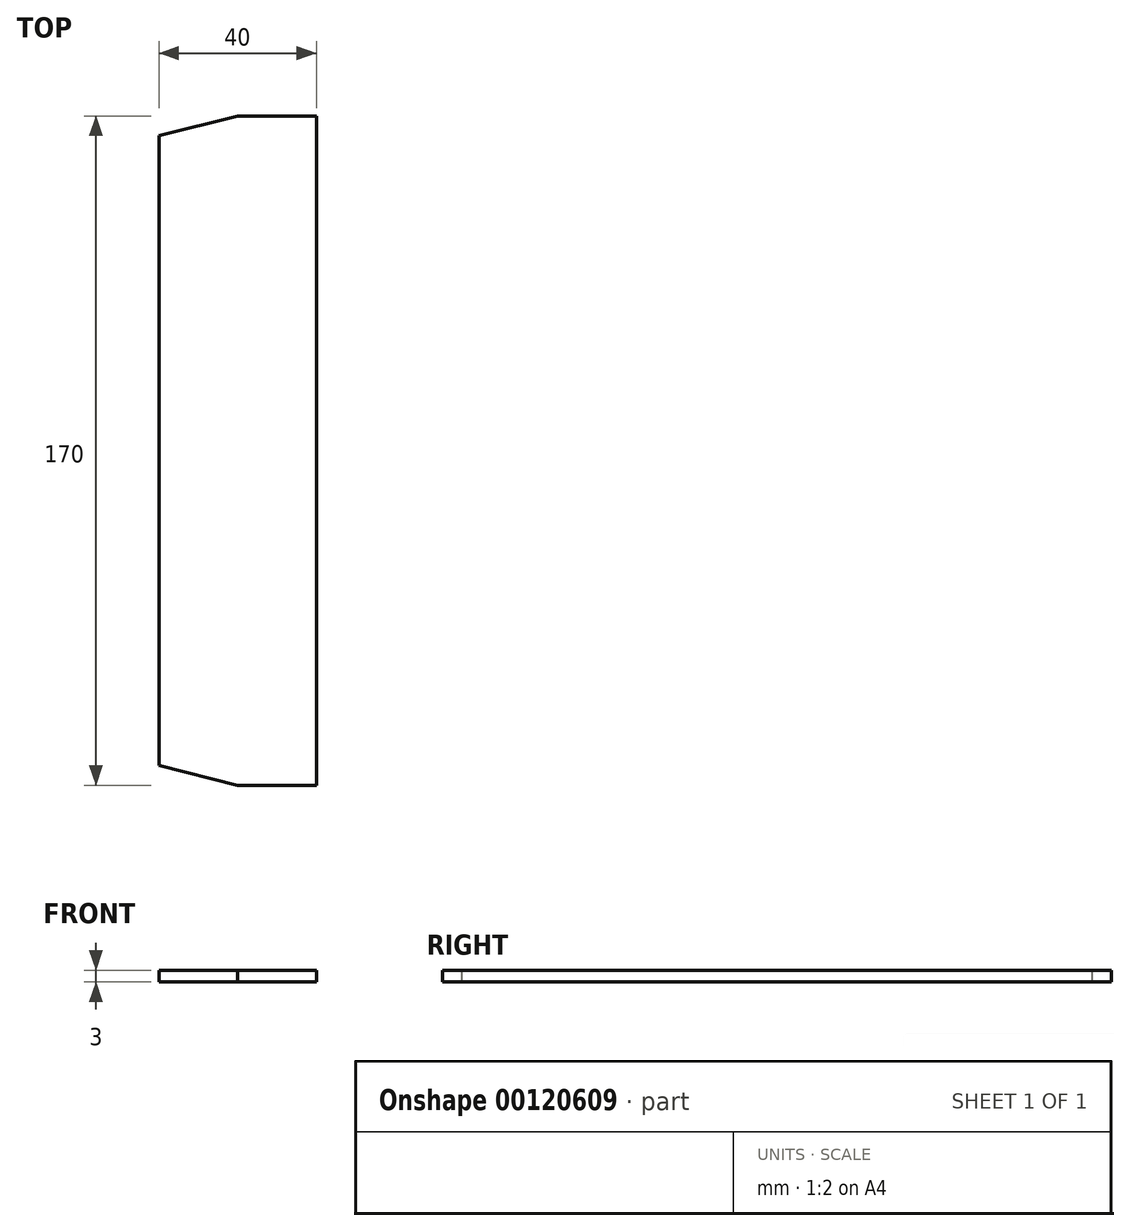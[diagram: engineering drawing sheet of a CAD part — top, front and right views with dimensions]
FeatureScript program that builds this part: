
annotation { "Feature Type Name" : "Feature", "Feature Type Description" : "" }
export const myFeature = defineFeature(function(context is Context, id is Id, definition is map)
    precondition{}
    {
        {
            var Q0;
            Q0=qCreatedBy(makeId("Top.planeOp"),FACE);
            var sketch = newSketch(context, id + "F0", { "sketchPlane" : qUnion([Q0])});
            skLineSegment(sketch, "E0.bottom", {"start": v(-59.55, 85.54) * mm, "end": v(-19.55, 85.54) * mm});
            skLineSegment(sketch, "E0.top", {"start": v(-59.55, -84.46) * mm, "end": v(-19.55, -84.46) * mm});
            skLineSegment(sketch, "E0.left", {"start": v(-59.55, 85.54) * mm, "end": v(-59.55, -84.46) * mm});
            skLineSegment(sketch, "E0.right", {"start": v(-19.55, 85.54) * mm, "end": v(-19.55, -84.46) * mm});
            skSolve(sketch);
        }
        {
            var Q0;
            Q0=makeQuery(id+"F0.imprint","IMPRINT",FACE,{"disambiguationData":[TD([[makeQuery(id+"F0.imprint","IMPRINT",EDGE,{"derivedFrom":sQuery(id+"F0.wireOp",EDGE,"E0.bottom")}),-1.0]])]});
            extrude(context, id + "F1", {"entities" : qUnion([Q0]), "depth" : 3 * mm});
        }
        {
            var Q0;
            Q0=makeQuery(id+"F1.opExtrude","SWEPT_EDGE",EDGE,{"disambiguationData":[OSD([sQuery(id+"F0.wireOp",EDGE,"E0.top"),sQuery(id+"F0.wireOp",EDGE,"E0.left")])]});
            chamfer(context, id + "F2", {"entities" : qUnion([Q0]), "chamferType" : ChamferType.TWO_OFFSETS, "width1" : 20 * mm, "oppositeDirection" : false, "width2" : 5 * mm, "tangentPropagation" : true});
        }
        {
            var Q0;
            Q0=makeQuery(id+"F1.opExtrude","SWEPT_EDGE",EDGE,{"disambiguationData":[OSD([sQuery(id+"F0.wireOp",EDGE,"E0.bottom"),sQuery(id+"F0.wireOp",EDGE,"E0.left")])]});
            chamfer(context, id + "F3", {"entities" : qUnion([Q0]), "chamferType" : ChamferType.TWO_OFFSETS, "width1" : 5 * mm, "oppositeDirection" : false, "width2" : 20 * mm, "tangentPropagation" : true});
        }
    });
